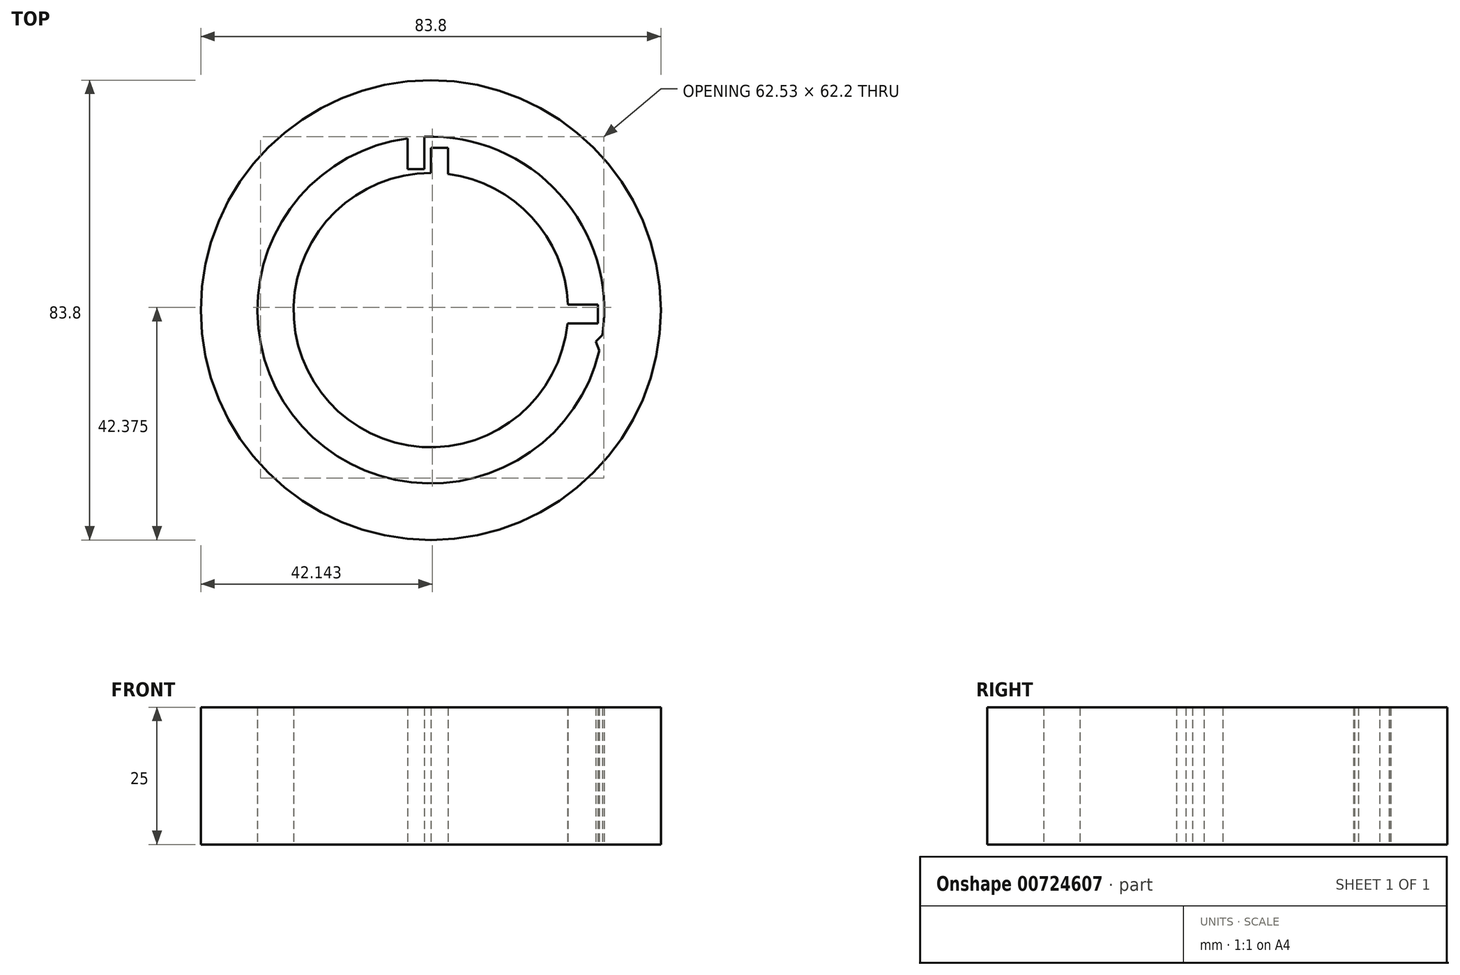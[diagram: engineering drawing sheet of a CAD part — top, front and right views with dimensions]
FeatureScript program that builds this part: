
annotation { "Feature Type Name" : "Feature", "Feature Type Description" : "" }
export const myFeature = defineFeature(function(context is Context, id is Id, definition is map)
    precondition{}
    {
        {
            var Q0;
            Q0=qCreatedBy(makeId("Top.planeOp"),FACE);
            var sketch = newSketch(context, id + "F0", { "sketchPlane" : qUnion([Q0])});
            skCircle(sketch, "E0", {"center": v(0, 0) * mm, "radius": 25 * mm});
            skCircle(sketch, "E1.0", {"center": v(0, 0) * mm, "radius": 41.9 * mm});
            skCircle(sketch, "E2.0", {"center": v(0, 0) * mm, "radius": 31.6 * mm});
            skLineSegment(sketch, "E3.bottom", {"start": v(-1.2, 32.82) * mm, "end": v(-4.23, 32.82) * mm});
            skLineSegment(sketch, "E3.top", {"start": v(-1.2, 25.69) * mm, "end": v(-4.23, 25.69) * mm});
            skLineSegment(sketch, "E3.left", {"start": v(-1.2, 32.82) * mm, "end": v(-1.2, 25.69) * mm});
            skLineSegment(sketch, "E3.right", {"start": v(-4.23, 32.82) * mm, "end": v(-4.23, 25.69) * mm});
            skLineSegment(sketch, "E4.bottom", {"start": v(3.12, 22.84) * mm, "end": v(0, 22.84) * mm});
            skLineSegment(sketch, "E4.top", {"start": v(3.12, 29.6) * mm, "end": v(0, 29.6) * mm});
            skLineSegment(sketch, "E4.left", {"start": v(3.12, 22.84) * mm, "end": v(3.12, 29.6) * mm});
            skLineSegment(sketch, "E4.right", {"start": v(0, 22.84) * mm, "end": v(0, 29.6) * mm});
            skLineSegment(sketch, "E5.bottom", {"start": v(23.48, -2.41) * mm, "end": v(30.42, -2.41) * mm});
            skLineSegment(sketch, "E5.top", {"start": v(23.48, 1.03) * mm, "end": v(30.42, 1.03) * mm});
            skLineSegment(sketch, "E5.left", {"start": v(23.48, -2.41) * mm, "end": v(23.48, 1.03) * mm});
            skLineSegment(sketch, "E5.right", {"start": v(30.42, -2.41) * mm, "end": v(30.42, 1.03) * mm});
            skLineSegment(sketch, "E6", {"start": v(31.28, -4.5) * mm, "end": v(30.04, -5.74) * mm});
            skLineSegment(sketch, "E7", {"start": v(30.04, -5.74) * mm, "end": v(30.72, -7.4) * mm});
            skSolve(sketch);
        }
        {
            var Q0;
            {var subQ5=sQuery(id+"F0.wireOp",EDGE,"E5.right");Q0=makeQuery(id+"F0.imprint","IMPRINT",FACE,{"disambiguationData":[TD([[makeQuery(id+"F0.imprint","IMPRINT",EDGE,{"derivedFrom":subQ5}),1.0]])]});}
            var Q1;
            {var subQ1=sQuery(id+"F0.wireOp",EDGE,"E4.bottom");Q1=makeQuery(id+"F0.imprint","IMPRINT",FACE,{"disambiguationData":[TD([[makeQuery(id+"F0.imprint","IMPRINT",EDGE,{"derivedFrom":subQ1}),1.0]])]});}
            var Q2;
            {var subQ5=sQuery(id+"F0.wireOp",EDGE,"E5.left");Q2=makeQuery(id+"F0.imprint","IMPRINT",FACE,{"disambiguationData":[TD([[makeQuery(id+"F0.imprint","IMPRINT",EDGE,{"derivedFrom":subQ5}),-1.0]])]});}
            var Q3;
            {var subQ5=sQuery(id+"F0.wireOp",EDGE,"E4.bottom");Q3=makeQuery(id+"F0.imprint","IMPRINT",FACE,{"disambiguationData":[TD([[makeQuery(id+"F0.imprint","IMPRINT",EDGE,{"derivedFrom":subQ5}),-1.0]])]});}
            var Q4;
            {var subQ5=sQuery(id+"F0.wireOp",EDGE,"E4.top");Q4=makeQuery(id+"F0.imprint","IMPRINT",FACE,{"disambiguationData":[TD([[makeQuery(id+"F0.imprint","IMPRINT",EDGE,{"derivedFrom":subQ5}),1.0]])]});}
            extrude(context, id + "F1", {"entities" : qUnion([Q0, Q1, Q2, Q3, Q4]), "depth" : 25 * mm, "offsetDistance" : 25 * mm});
        }
        {
            var Q0;
            Q0=makeQuery(id+"F0.imprint","IMPRINT",FACE,{"disambiguationData":[TD([[makeQuery(id+"F0.imprint","IMPRINT",EDGE,{"derivedFrom":sQuery(id+"F0.wireOp",EDGE,"E1.0")}),1.0]])]});
            var Q1;
            {var subQ5=sQuery(id+"F0.wireOp",EDGE,"QqlL2kxn-1rAj-tp0H-2rdO-hha56KXtwFgz.left");Q1=makeQuery(id+"F0.imprint","IMPRINT",FACE,{"disambiguationData":[TD([[makeQuery(id+"F0.imprint","IMPRINT",EDGE,{"derivedFrom":subQ5}),1.0]])]});}
            var Q2;
            {var subQ5=sQuery(id+"F0.wireOp",EDGE,"QqlL2kxn-1rAj-tp0H-2rdO-hha56KXtwFgz.right");Q2=makeQuery(id+"F0.imprint","IMPRINT",FACE,{"disambiguationData":[TD([[makeQuery(id+"F0.imprint","IMPRINT",EDGE,{"derivedFrom":subQ5}),-1.0]])]});}
            var Q3;
            {var subQ5=sQuery(id+"F0.wireOp",EDGE,"E3.bottom");Q3=makeQuery(id+"F0.imprint","IMPRINT",FACE,{"disambiguationData":[TD([[makeQuery(id+"F0.imprint","IMPRINT",EDGE,{"derivedFrom":subQ5}),1.0]])]});}
            var Q4;
            {var subQ5=sQuery(id+"F0.wireOp",EDGE,"E3.top");Q4=makeQuery(id+"F0.imprint","IMPRINT",FACE,{"disambiguationData":[TD([[makeQuery(id+"F0.imprint","IMPRINT",EDGE,{"derivedFrom":subQ5}),-1.0]])]});}
            var Q5;
            {var subQ0=sQuery(id+"F0.wireOp",EDGE,"E6");Q5=makeQuery(id+"F0.imprint","IMPRINT",FACE,{"disambiguationData":[TD([[makeQuery(id+"F0.imprint","IMPRINT",EDGE,{"derivedFrom":subQ0}),1.0]])]});}
            extrude(context, id + "F2", {"entities" : qUnion([Q0, Q1, Q2, Q3, Q4, Q5]), "depth" : 25 * mm, "offsetDistance" : 25 * mm});
        }
    });
